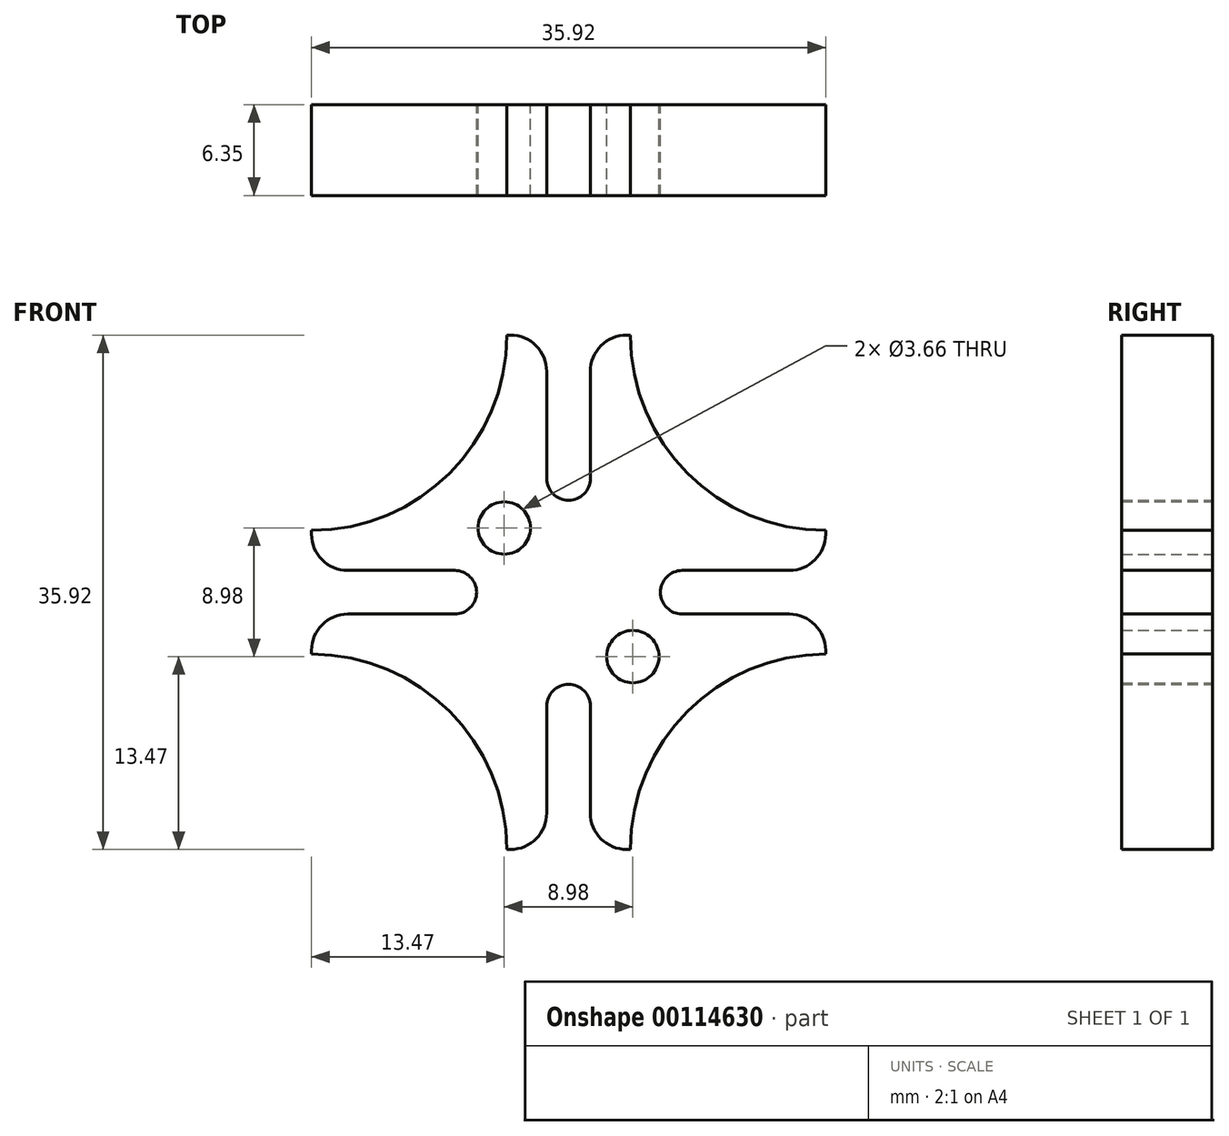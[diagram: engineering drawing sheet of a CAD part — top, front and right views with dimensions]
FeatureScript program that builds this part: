
annotation { "Feature Type Name" : "Feature", "Feature Type Description" : "" }
export const myFeature = defineFeature(function(context is Context, id is Id, definition is map)
    precondition{}
    {
        {
            var Q0;
            Q0=qCreatedBy(makeId("Front.planeOp"),FACE);
            var sketch = newSketch(context, id + "F0", { "sketchPlane" : qUnion([Q0])});
            skLineSegment(sketch, "E0.bottom", {"start": v(17.96, -17.96) * mm, "end": v(-17.96, -17.96) * mm, "construction": true});
            skLineSegment(sketch, "E0.top", {"start": v(17.96, 17.96) * mm, "end": v(-17.96, 17.96) * mm, "construction": true});
            skLineSegment(sketch, "E0.left", {"start": v(17.96, -17.96) * mm, "end": v(17.96, 17.96) * mm, "construction": true});
            skLineSegment(sketch, "E0.right", {"start": v(-17.96, -17.96) * mm, "end": v(-17.96, 17.96) * mm, "construction": true});
            skPoint(sketch, "E0.middle", {"position": v(0, 0) * mm});
            skPoint(sketch, "E1", {"position": v(-17.96, 0) * mm});
            skPoint(sketch, "E2", {"position": v(-17.96, 1.52) * mm});
            skPoint(sketch, "E3", {"position": v(-17.96, -1.52) * mm});
            skLineSegment(sketch, "E4", {"start": v(0, 0) * mm, "end": v(0, -23.32) * mm, "construction": true});
            skLineSegment(sketch, "E5", {"start": v(0, 0) * mm, "end": v(26.59, 0) * mm, "construction": true});
            skPoint(sketch, "E6", {"position": v(0, -17.96) * mm});
            skPoint(sketch, "E7", {"position": v(1.52, -17.96) * mm});
            skPoint(sketch, "E8", {"position": v(-1.52, -17.96) * mm});
            skPoint(sketch, "E9.MirrorP", {"position": v(17.96, 1.52) * mm});
            skPoint(sketch, "E10.MirrorP", {"position": v(17.96, -1.52) * mm});
            skPoint(sketch, "E11.MirrorP", {"position": v(1.52, 17.96) * mm});
            skPoint(sketch, "E12.MirrorP", {"position": v(-1.52, 17.96) * mm});
            skLineSegment(sketch, "E13", {"start": v(-1.52, -17.96) * mm, "end": v(-1.52, -7.95) * mm});
            skLineSegment(sketch, "E14", {"start": v(1.52, -17.96) * mm, "end": v(1.52, -7.95) * mm});
            skLineSegment(sketch, "E15", {"start": v(-17.96, 1.52) * mm, "end": v(-7.95, 1.52) * mm});
            skLineSegment(sketch, "E16", {"start": v(-17.96, -1.52) * mm, "end": v(-7.95, -1.52) * mm});
            skArc(sketch, "E17", {"start": v(-7.95, 1.52) * mm, "mid": v(-6.42, 0) * mm, "end": v(-7.95, -1.52) * mm});
            skArc(sketch, "E18", {"start": v(-1.52, -7.95) * mm, "mid": v(0, -6.42) * mm, "end": v(1.52, -7.95) * mm});
            skLineSegment(sketch, "E19", {"start": v(0, -17.96) * mm, "end": v(0, -6.42) * mm, "construction": true});
            skLineSegment(sketch, "E20.MirrorCS", {"start": v(1.52, 17.96) * mm, "end": v(1.52, 7.95) * mm});
            skLineSegment(sketch, "E21.MirrorCS", {"start": v(-1.52, 17.96) * mm, "end": v(-1.52, 7.95) * mm});
            skArc(sketch, "E22.MirrorCS", {"start": v(-1.52, 7.95) * mm, "mid": v(0, 6.42) * mm, "end": v(1.52, 7.95) * mm});
            skLineSegment(sketch, "E23.MirrorCS", {"start": v(17.96, -1.52) * mm, "end": v(7.95, -1.52) * mm});
            skLineSegment(sketch, "E24.MirrorCS", {"start": v(17.96, 1.52) * mm, "end": v(7.95, 1.52) * mm});
            skArc(sketch, "E25.MirrorCS", {"start": v(7.95, 1.52) * mm, "mid": v(6.42, 0) * mm, "end": v(7.95, -1.52) * mm});
            skLineSegment(sketch, "E26", {"start": v(0, 0) * mm, "end": v(17.96, 17.96) * mm, "construction": true});
            skCircle(sketch, "E27", {"center": v(17.96, 17.96) * mm, "radius": 13.64 * mm, "construction": true});
            skArc(sketch, "E28", {"start": v(4.32, 17.96) * mm, "mid": v(8.31, 8.31) * mm, "end": v(17.96, 4.32) * mm});
            skArc(sketch, "E29.MirrorCS", {"start": v(4.32, -17.96) * mm, "mid": v(8.31, -8.31) * mm, "end": v(17.96, -4.32) * mm});
            skArc(sketch, "E30.MirrorCS", {"start": v(-4.32, -17.96) * mm, "mid": v(-8.31, -8.31) * mm, "end": v(-17.96, -4.32) * mm});
            skArc(sketch, "E31.MirrorCS", {"start": v(-4.32, 17.96) * mm, "mid": v(-8.31, 8.31) * mm, "end": v(-17.96, 4.32) * mm});
            skLineSegment(sketch, "E32", {"start": v(-17.96, 4.32) * mm, "end": v(-17.96, 1.52) * mm});
            skLineSegment(sketch, "E33", {"start": v(-17.96, -1.52) * mm, "end": v(-17.96, -4.32) * mm});
            skLineSegment(sketch, "E34", {"start": v(-4.32, -17.96) * mm, "end": v(-1.52, -17.96) * mm});
            skLineSegment(sketch, "E35", {"start": v(1.52, -17.96) * mm, "end": v(4.32, -17.96) * mm});
            skLineSegment(sketch, "E36", {"start": v(17.96, -4.32) * mm, "end": v(17.96, -1.52) * mm});
            skLineSegment(sketch, "E37", {"start": v(17.96, 1.52) * mm, "end": v(17.96, 4.32) * mm});
            skLineSegment(sketch, "E38", {"start": v(4.32, 17.96) * mm, "end": v(1.52, 17.96) * mm});
            skLineSegment(sketch, "E39", {"start": v(-1.52, 17.96) * mm, "end": v(-4.32, 17.96) * mm});
            skCircle(sketch, "E40", {"center": v(0, 0) * mm, "radius": 18.47 * mm, "construction": true});
            skLineSegment(sketch, "E41", {"start": v(-17.96, 0) * mm, "end": v(-7.95, 0) * mm, "construction": true});
            skLineSegment(sketch, "E42", {"start": v(0, 0) * mm, "end": v(4.5, -4.5) * mm, "construction": true});
            skCircle(sketch, "E43", {"center": v(4.5, -4.5) * mm, "radius": 1.83 * mm});
            skLineSegment(sketch, "E44.MirrorCS", {"start": v(0, 0) * mm, "end": v(-4.5, 4.5) * mm, "construction": true});
            skCircle(sketch, "E45.MirrorC", {"center": v(-4.5, 4.5) * mm, "radius": 1.83 * mm});
            skSolve(sketch);
        }
        {
            var Q0;
            Q0 = qSketchRegion(id + "F0", true);
            extrude(context, id + "F1", {"entities" : qUnion([Q0]), "depth" : 6.35 * mm});
        }
        {
            var Q0;
            Q0=makeQuery(id+"F1.opExtrude","SWEPT_EDGE",EDGE,{"disambiguationData":[OSD([sQuery(id+"F0.wireOp",EDGE,"E13"),sQuery(id+"F0.wireOp",EDGE,"E34")])]});
            var Q1;
            Q1=makeQuery(id+"F1.opExtrude","SWEPT_EDGE",EDGE,{"disambiguationData":[OSD([sQuery(id+"F0.wireOp",EDGE,"E14"),sQuery(id+"F0.wireOp",EDGE,"E35")])]});
            var Q2;
            Q2=makeQuery(id+"F1.opExtrude","SWEPT_EDGE",EDGE,{"disambiguationData":[OSD([sQuery(id+"F0.wireOp",EDGE,"E15"),sQuery(id+"F0.wireOp",EDGE,"E32")])]});
            var Q3;
            Q3=makeQuery(id+"F1.opExtrude","SWEPT_EDGE",EDGE,{"disambiguationData":[OSD([sQuery(id+"F0.wireOp",EDGE,"E24.MirrorCS"),sQuery(id+"F0.wireOp",EDGE,"E37")])]});
            var Q4;
            Q4=makeQuery(id+"F1.opExtrude","SWEPT_EDGE",EDGE,{"disambiguationData":[OSD([sQuery(id+"F0.wireOp",EDGE,"E16"),sQuery(id+"F0.wireOp",EDGE,"E33")])]});
            var Q5;
            Q5=makeQuery(id+"F1.opExtrude","SWEPT_EDGE",EDGE,{"disambiguationData":[OSD([sQuery(id+"F0.wireOp",EDGE,"E23.MirrorCS"),sQuery(id+"F0.wireOp",EDGE,"E36")])]});
            var Q6;
            Q6=makeQuery(id+"F1.opExtrude","SWEPT_EDGE",EDGE,{"disambiguationData":[OSD([sQuery(id+"F0.wireOp",EDGE,"E20.MirrorCS"),sQuery(id+"F0.wireOp",EDGE,"E38")])]});
            var Q7;
            Q7=makeQuery(id+"F1.opExtrude","SWEPT_EDGE",EDGE,{"disambiguationData":[OSD([sQuery(id+"F0.wireOp",EDGE,"E21.MirrorCS"),sQuery(id+"F0.wireOp",EDGE,"E39")])]});
            fillet(context, id + "F2", {"entities" : qUnion([Q0, Q1, Q2, Q3, Q4, Q5, Q6, Q7]), "radius" : 2.54 * mm, "tangentPropagation" : true, "allowEdgeOverflow" : false});
        }
    });
